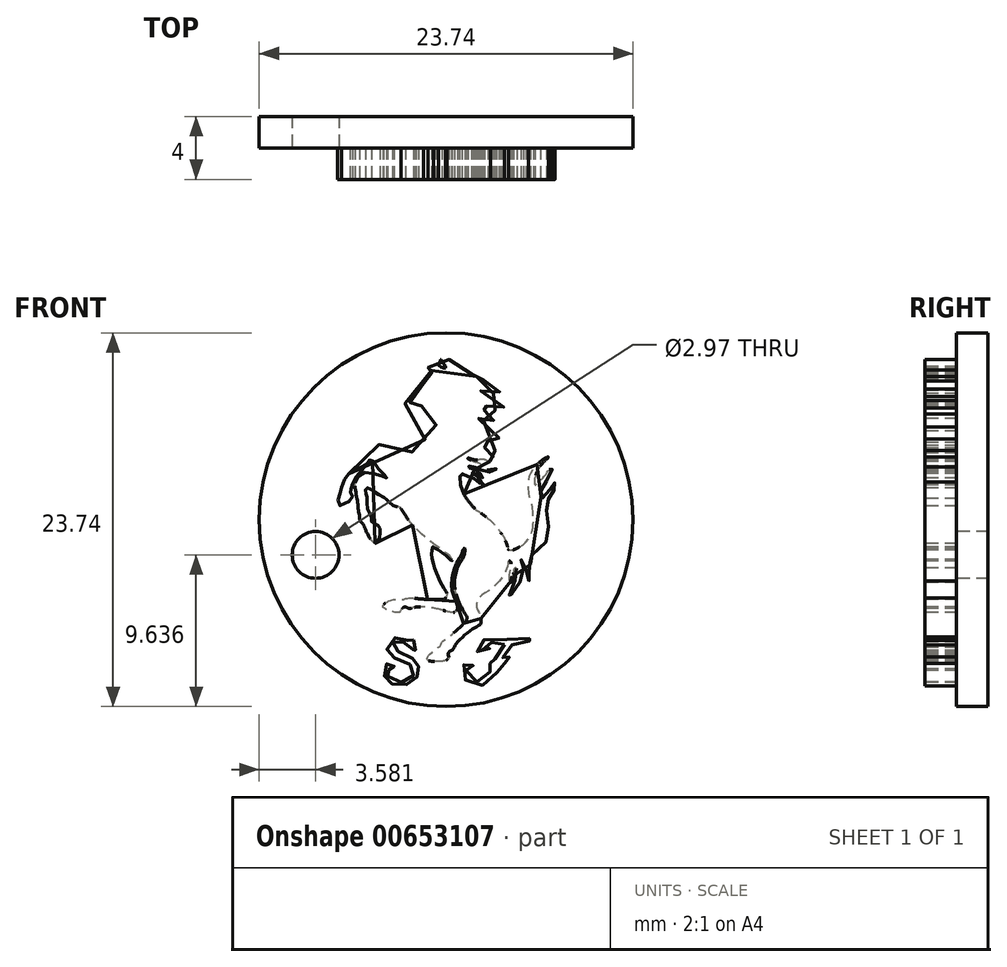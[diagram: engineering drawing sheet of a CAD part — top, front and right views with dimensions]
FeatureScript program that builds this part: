
annotation { "Feature Type Name" : "Feature", "Feature Type Description" : "" }
export const myFeature = defineFeature(function(context is Context, id is Id, definition is map)
    precondition{}
    {
        {
            var Q0;
            Q0=qCreatedBy(makeId("Front.planeOp"),FACE);
            var sketch = newSketch(context, id + "F0", { "sketchPlane" : qUnion([Q0])});
            skCircle(sketch, "E0", {"center": v(-6.3, 17.6) * mm, "radius": 11.87 * mm});
            skSolve(sketch);
        }
        {
            var Q0;
            Q0=qCreatedBy(makeId("Front.planeOp"),FACE);
            var sketch = newSketch(context, id + "F1", { "sketchPlane" : qUnion([Q0])});
            skFitSpline(sketch, "E1", {"points": [v(-12.5, 20.52) * mm, v(-12.32, 20.83) * mm, v(-12.29, 20.92) * mm, v(-11.96, 21.5) * mm, v(-11.74, 21.89) * mm, v(-11.58, 22.13) * mm, v(-11.5, 22.28) * mm, v(-11.38, 22.4) * mm, v(-11.23, 22.5) * mm, v(-11.09, 22.52) * mm, v(-11, 22.52) * mm, v(-10.9, 22.5) * mm, v(-10.7, 22.45) * mm, v(-10.6, 22.38) * mm, v(-10.51, 22.33) * mm, v(-10.41, 22.25) * mm, v(-10.33, 22.16) * mm, v(-10.27, 22.08) * mm, v(-10.24, 22.05) * mm, v(-10.22, 22.03) * mm, v(-10.1, 21.96) * mm, v(-9.68, 21.67) * mm, v(-9.47, 21.52) * mm, v(-9.3, 21.41) * mm, v(-9.27, 21.38) * mm, v(-9.25, 21.37) * mm, v(-9.24, 21.38) * mm, v(-9.06, 21.53) * mm, v(-8.92, 21.64) * mm, v(-8.83, 21.7) * mm, v(-8.55, 21.86) * mm, v(-8.37, 21.93) * mm, v(-8.25, 22) * mm, v(-8.17, 22.07) * mm, v(-8.05, 22.2) * mm, v(-7.95, 22.35) * mm, v(-7.9, 22.42) * mm, v(-7.84, 22.5) * mm, v(-7.77, 22.57) * mm, v(-7.75, 22.6) * mm, v(-7.62, 22.7) * mm, v(-7.51, 22.82) * mm, v(-7.47, 22.88) * mm, v(-7.3, 23.07) * mm, v(-7.18, 23.22) * mm, v(-7.1, 23.34) * mm, v(-7.01, 23.47) * mm, v(-6.9, 23.7) * mm, v(-6.8, 23.89) * mm, v(-6.65, 24.26) * mm, v(-6.6, 24.4) * mm, v(-6.57, 24.48) * mm, v(-6.57, 24.56) * mm, v(-6.59, 24.6) * mm, v(-6.63, 24.66) * mm, v(-6.67, 24.69) * mm, v(-6.75, 24.66) * mm, v(-6.88, 24.64) * mm, v(-6.89, 24.64) * mm, v(-7.03, 24.64) * mm, v(-7.24, 24.7) * mm, v(-7.32, 24.71) * mm, v(-7.62, 24.8) * mm, v(-7.8, 24.82) * mm, v(-7.81, 24.82) * mm, v(-7.9, 24.83) * mm, v(-8.1, 24.84) * mm, v(-8.32, 24.76) * mm, v(-8.43, 24.7) * mm, v(-8.54, 24.68) * mm, v(-8.67, 24.68) * mm, v(-8.76, 24.71) * mm, v(-8.85, 24.78) * mm, v(-8.87, 24.83) * mm, v(-8.83, 24.88) * mm, v(-8.76, 24.9) * mm, v(-8.7, 24.9) * mm, v(-8.57, 24.94) * mm, v(-8.45, 24.98) * mm, v(-8.38, 25.02) * mm, v(-8.36, 25.06) * mm, v(-8.37, 25.09) * mm, v(-8.4, 25.1) * mm, v(-8.45, 25.11) * mm, v(-8.5, 25.1) * mm, v(-8.63, 25.05) * mm, v(-8.92, 24.98) * mm, v(-9.08, 24.98) * mm, v(-9.1, 24.99) * mm, v(-9.14, 25.03) * mm, v(-9.16, 25.11) * mm, v(-9.17, 25.2) * mm, v(-9.18, 25.36) * mm, v(-9.12, 25.5) * mm, v(-8.97, 25.73) * mm, v(-8.88, 25.87) * mm, v(-8.68, 25.99) * mm, v(-8.43, 26.02) * mm, v(-8.22, 26.07) * mm, v(-7.93, 26.18) * mm, v(-7.63, 26.3) * mm, v(-7.48, 26.39) * mm, v(-7.25, 26.53) * mm, v(-7.08, 26.62) * mm, v(-6.95, 26.67) * mm, v(-6.86, 26.7) * mm, v(-6.82, 26.7) * mm, v(-6.8, 26.73) * mm, v(-6.8, 26.75) * mm, v(-6.81, 26.77) * mm, v(-6.84, 26.77) * mm, v(-6.93, 26.77) * mm, v(-6.98, 26.76) * mm, v(-7, 26.77) * mm, v(-7, 26.8) * mm, v(-6.98, 26.81) * mm, v(-6.95, 26.82) * mm, v(-6.91, 26.83) * mm, v(-6.9, 26.86) * mm, v(-6.9, 26.88) * mm, v(-6.91, 26.88) * mm, v(-6.95, 26.88) * mm, v(-7, 26.88) * mm, v(-7.05, 26.88) * mm, v(-7.1, 26.9) * mm, v(-7.24, 26.95) * mm, v(-7.36, 26.98) * mm, v(-7.43, 27) * mm, v(-7.5, 27) * mm, v(-7.67, 26.97) * mm, v(-7.7, 26.96) * mm, v(-7.73, 26.96) * mm, v(-7.74, 26.97) * mm, v(-7.75, 27) * mm, v(-7.75, 27.02) * mm, v(-7.7, 27.04) * mm, v(-7.63, 27.07) * mm, v(-7.54, 27.1) * mm, v(-7.34, 27.1) * mm, v(-7.28, 27.08) * mm, v(-7.2, 27.09) * mm, v(-7.16, 27.1) * mm, v(-7.12, 27.13) * mm, v(-7.12, 27.14) * mm, v(-7.12, 27.14) * mm, v(-7.14, 27.15) * mm, v(-7.17, 27.16) * mm, v(-7.24, 27.16) * mm, v(-7.28, 27.18) * mm, v(-7.42, 27.22) * mm, v(-7.44, 27.24) * mm, v(-7.44, 27.27) * mm, v(-7.42, 27.28) * mm, v(-7.38, 27.28) * mm, v(-7.32, 27.29) * mm, v(-7.27, 27.29) * mm, v(-7.2, 27.3) * mm, v(-7.1, 27.32) * mm, v(-6.98, 27.32) * mm, v(-6.87, 27.3) * mm, v(-6.77, 27.27) * mm, v(-6.66, 27.22) * mm, v(-6.48, 27.14) * mm, v(-6.34, 27.12) * mm, v(-6.25, 27.13) * mm, v(-6.18, 27.18) * mm, v(-6.16, 27.2) * mm, v(-6.17, 27.26) * mm, v(-6.23, 27.34) * mm, v(-6.23, 27.5) * mm, v(-6.19, 27.59) * mm, v(-6.12, 27.78) * mm, v(-6.12, 27.79) * mm, v(-6.1, 27.78) * mm, v(-6.07, 27.74) * mm, v(-5.99, 27.64) * mm, v(-5.88, 27.57) * mm, v(-5.8, 27.5) * mm, v(-5.77, 27.48) * mm, v(-5.68, 27.41) * mm, v(-5.59, 27.32) * mm, v(-5.52, 27.25) * mm, v(-5.47, 27.18) * mm, v(-5.45, 27.14) * mm, v(-5.44, 27.12) * mm, v(-5.42, 27.12) * mm, v(-5.28, 27.12) * mm, v(-5.27, 27.12) * mm, v(-5.11, 27.1) * mm, v(-5.1, 27.1) * mm, v(-5.04, 27.1) * mm, v(-5, 27.07) * mm, v(-4.9, 27.02) * mm, v(-4.8, 26.94) * mm, v(-4.79, 26.93) * mm, v(-4.71, 26.85) * mm, v(-4.62, 26.74) * mm, v(-4.57, 26.72) * mm, v(-4.5, 26.7) * mm, v(-4.37, 26.7) * mm, v(-4.12, 26.7) * mm, v(-3.95, 26.7) * mm, v(-3.8, 26.7) * mm, v(-3.7, 26.67) * mm, v(-3.64, 26.63) * mm, v(-3.53, 26.56) * mm, v(-3.5, 26.52) * mm, v(-3.5, 26.49) * mm, v(-3.5, 26.46) * mm, v(-3.52, 26.43) * mm, v(-3.57, 26.42) * mm, v(-3.64, 26.45) * mm, v(-3.7, 26.48) * mm, v(-3.73, 26.5) * mm, v(-3.77, 26.5) * mm, v(-3.83, 26.5) * mm, v(-3.87, 26.48) * mm, v(-3.94, 26.46) * mm, v(-4, 26.44) * mm, v(-4.26, 26.36) * mm, v(-4.3, 26.33) * mm, v(-4.32, 26.32) * mm, v(-4.32, 26.3) * mm, v(-4.3, 26.29) * mm, v(-4.28, 26.28) * mm, v(-4.2, 26.27) * mm, v(-4.2, 26.27) * mm, v(-4.13, 26.25) * mm, v(-4.02, 26.22) * mm, v(-3.87, 26.15) * mm, v(-3.76, 26.08) * mm, v(-3.65, 26) * mm, v(-3.54, 25.94) * mm, v(-3.5, 25.92) * mm, v(-3.42, 25.91) * mm, v(-3.3, 25.9) * mm, v(-3.14, 25.86) * mm, v(-3.03, 25.8) * mm, v(-2.92, 25.72) * mm, v(-2.86, 25.67) * mm, v(-2.86, 25.67) * mm, v(-2.79, 25.6) * mm, v(-2.78, 25.6) * mm, v(-2.72, 25.57) * mm, v(-2.66, 25.53) * mm, v(-2.62, 25.5) * mm, v(-2.6, 25.47) * mm, v(-2.6, 25.46) * mm, v(-2.62, 25.44) * mm, v(-2.65, 25.44) * mm, v(-2.72, 25.45) * mm, v(-2.82, 25.49) * mm, v(-2.9, 25.54) * mm, v(-2.99, 25.59) * mm, v(-3.02, 25.6) * mm, v(-3.07, 25.62) * mm, v(-3.16, 25.62) * mm, v(-3.16, 25.62) * mm, v(-3.25, 25.62) * mm, v(-3.39, 25.6) * mm, v(-3.63, 25.62) * mm, v(-3.98, 25.74) * mm, v(-4.19, 25.8) * mm, v(-4.3, 25.8) * mm, v(-4.3, 25.8) * mm, v(-4.31, 25.76) * mm, v(-4.28, 25.7) * mm, v(-4.16, 25.64) * mm, v(-4, 25.56) * mm, v(-3.93, 25.52) * mm, v(-3.81, 25.41) * mm, v(-3.75, 25.32) * mm, v(-3.67, 25.24) * mm, v(-3.51, 25.18) * mm, v(-3.32, 25.17) * mm, v(-3.07, 25.1) * mm, v(-2.85, 24.98) * mm, v(-2.78, 24.92) * mm, v(-2.68, 24.82) * mm, v(-2.64, 24.75) * mm, v(-2.65, 24.72) * mm, v(-2.67, 24.68) * mm, v(-2.7, 24.68) * mm, v(-2.72, 24.7) * mm, v(-2.77, 24.77) * mm, v(-2.83, 24.83) * mm, v(-2.92, 24.9) * mm, v(-3.02, 24.93) * mm, v(-3.12, 24.94) * mm, v(-3.23, 24.9) * mm, v(-3.45, 24.88) * mm, v(-3.57, 24.9) * mm, v(-3.75, 24.98) * mm, v(-3.88, 25.09) * mm, v(-3.9, 25.1) * mm, v(-3.94, 25.12) * mm, v(-3.95, 25.12) * mm, v(-3.96, 25.1) * mm, v(-3.96, 25.06) * mm, v(-3.9, 25) * mm, v(-3.76, 24.86) * mm, v(-3.76, 24.85) * mm, v(-3.65, 24.75) * mm, v(-3.57, 24.7) * mm, v(-3.51, 24.7) * mm, v(-3.41, 24.66) * mm, v(-3.27, 24.6) * mm, v(-3.15, 24.53) * mm, v(-3.1, 24.49) * mm, v(-3.07, 24.47) * mm, v(-3.02, 24.46) * mm, v(-2.97, 24.45) * mm, v(-2.89, 24.45) * mm, v(-2.88, 24.44) * mm, v(-2.87, 24.42) * mm, v(-2.88, 24.39) * mm, v(-2.9, 24.37) * mm, v(-2.97, 24.33) * mm, v(-3.13, 24.33) * mm, v(-3.26, 24.38) * mm, v(-3.5, 24.45) * mm, v(-3.7, 24.5) * mm, v(-3.93, 24.6) * mm, v(-4.07, 24.68) * mm, v(-4.13, 24.7) * mm, v(-4.25, 24.7) * mm, v(-4.3, 24.68) * mm, v(-4.3, 24.68) * mm, v(-4.32, 24.65) * mm, v(-4.32, 24.62) * mm, v(-4.28, 24.6) * mm, v(-4.22, 24.57) * mm, v(-4.12, 24.55) * mm, v(-4.05, 24.53) * mm, v(-3.97, 24.5) * mm, v(-3.87, 24.44) * mm, v(-3.73, 24.36) * mm, v(-3.65, 24.3) * mm, v(-3.59, 24.23) * mm, v(-3.55, 24.14) * mm, v(-3.5, 24.07) * mm, v(-3.46, 24.01) * mm, v(-3.4, 23.98) * mm, v(-3.32, 23.93) * mm, v(-3.26, 23.89) * mm, v(-3.22, 23.84) * mm, v(-3.18, 23.79) * mm, v(-3.15, 23.73) * mm, v(-3.1, 23.68) * mm, v(-2.98, 23.62) * mm, v(-2.9, 23.6) * mm, v(-2.86, 23.55) * mm, v(-2.84, 23.5) * mm, v(-2.84, 23.5) * mm, v(-3.08, 23.5) * mm, v(-3.3, 23.65) * mm, v(-3.36, 23.7) * mm, v(-3.61, 23.77) * mm, v(-3.72, 23.81) * mm, v(-3.86, 23.88) * mm, v(-3.99, 23.94) * mm, v(-4.15, 24) * mm, v(-4.19, 24.03) * mm, v(-4.25, 24.04) * mm, v(-4.28, 24.03) * mm, v(-4.28, 24) * mm, v(-4.25, 23.94) * mm, v(-4.15, 23.82) * mm, v(-4.05, 23.74) * mm, v(-3.91, 23.65) * mm, v(-3.8, 23.58) * mm, v(-3.74, 23.54) * mm, v(-3.62, 23.43) * mm, v(-3.54, 23.32) * mm, v(-3.5, 23.25) * mm, v(-3.5, 23.18) * mm, v(-3.48, 23.13) * mm, v(-3.42, 23.05) * mm, v(-3.33, 23) * mm, v(-3.23, 22.95) * mm, v(-3.1, 22.92) * mm, v(-3, 22.88) * mm, v(-2.95, 22.8) * mm, v(-2.95, 22.78) * mm, v(-2.98, 22.76) * mm, v(-3.29, 22.74) * mm, v(-3.6, 22.9) * mm, v(-3.75, 23.06) * mm, v(-3.87, 23.12) * mm, v(-4.06, 23.15) * mm, v(-4.25, 23.23) * mm, v(-4.4, 23.23) * mm, v(-4.43, 23.2) * mm, v(-4.44, 23.16) * mm, v(-4.32, 23.1) * mm, v(-4.17, 23.03) * mm, v(-4, 22.82) * mm, v(-3.84, 22.7) * mm, v(-3.66, 22.61) * mm, v(-3.53, 22.5) * mm, v(-3.41, 22.33) * mm, v(-3.33, 22.22) * mm, v(-3.33, 22.19) * mm, v(-3.24, 22.09) * mm, v(-3.2, 22.05) * mm, v(-3.18, 22.02) * mm, v(-3.23, 22) * mm, v(-3.31, 22) * mm, v(-3.46, 22.15) * mm, v(-3.52, 22.2) * mm, v(-3.7, 22.27) * mm, v(-4.11, 22.48) * mm, v(-4.17, 22.5) * mm, v(-4.17, 22.47) * mm, v(-4.1, 22.37) * mm, v(-3.96, 22.27) * mm, v(-3.87, 22.2) * mm, v(-3.85, 22.17) * mm, v(-3.87, 22.15) * mm, v(-3.92, 22.14) * mm, v(-4, 22.15) * mm, v(-4.07, 22.19) * mm, v(-4.13, 22.23) * mm, v(-4.3, 22.3) * mm, v(-4.36, 22.3) * mm, v(-4.38, 22.3) * mm, v(-4.38, 22.28) * mm, v(-4.33, 22.2) * mm, v(-4.15, 22.1) * mm, v(-3.94, 22.06) * mm, v(-3.83, 22.01) * mm, v(-3.72, 21.93) * mm, v(-3.55, 21.8) * mm, v(-3.4, 21.74) * mm, v(-3.3, 21.72) * mm, v(-3.28, 21.69) * mm, v(-3.28, 21.62) * mm, v(-3.37, 21.6) * mm, v(-3.58, 21.62) * mm, v(-3.8, 21.67) * mm, v(-3.95, 21.77) * mm, v(-4.12, 21.83) * mm, v(-4.28, 21.83) * mm, v(-4.4, 21.8) * mm, v(-4.4, 21.77) * mm, v(-4.36, 21.75) * mm, v(-4.19, 21.74) * mm, v(-4.04, 21.7) * mm, v(-3.94, 21.67) * mm, v(-3.83, 21.6) * mm, v(-3.7, 21.47) * mm, v(-3.54, 21.35) * mm, v(-3.52, 21.32) * mm, v(-3.54, 21.3) * mm, v(-3.57, 21.28) * mm, v(-3.67, 21.32) * mm, v(-3.82, 21.4) * mm, v(-4.01, 21.43) * mm, v(-4.2, 21.4) * mm, v(-4.49, 21.4) * mm, v(-4.78, 21.48) * mm, v(-4.88, 21.52) * mm, v(-4.91, 21.52) * mm, v(-4.92, 21.5) * mm, v(-4.92, 21.47) * mm, v(-4.9, 21.45) * mm, v(-4.79, 21.4) * mm, v(-4.64, 21.34) * mm, v(-4.47, 21.27) * mm, v(-4.24, 21.2) * mm, v(-4.03, 21.06) * mm, v(-3.93, 20.95) * mm, v(-3.8, 20.82) * mm, v(-3.65, 20.75) * mm, v(-3.43, 20.76) * mm, v(-3.28, 20.8) * mm, v(-3.16, 20.88) * mm, v(-3.12, 20.9) * mm, v(-3.1, 20.89) * mm, v(-3.1, 20.87) * mm, v(-3.12, 20.81) * mm, v(-3.31, 20.68) * mm, v(-3.57, 20.63) * mm, v(-3.88, 20.67) * mm, v(-4.13, 20.79) * mm, v(-4.3, 20.86) * mm, v(-4.33, 20.86) * mm, v(-4.43, 20.9) * mm, v(-4.65, 20.94) * mm, v(-4.77, 20.97) * mm, v(-4.87, 21) * mm, v(-4.93, 21.01) * mm, v(-4.95, 21.01) * mm, v(-4.94, 20.98) * mm, v(-4.8, 20.9) * mm, v(-4.78, 20.9) * mm, v(-4.67, 20.86) * mm, v(-4.55, 20.82) * mm, v(-4.37, 20.72) * mm, v(-4.25, 20.63) * mm, v(-4.16, 20.54) * mm, v(-4, 20.4) * mm, v(-3.97, 20.36) * mm, v(-3.98, 20.27) * mm, v(-4, 20.26) * mm, v(-4.06, 20.29) * mm, v(-4.2, 20.4) * mm, v(-4.33, 20.5) * mm, v(-4.48, 20.55) * mm, v(-4.58, 20.57) * mm, v(-4.65, 20.58) * mm, v(-4.67, 20.58) * mm, v(-4.69, 20.56) * mm, v(-4.7, 20.54) * mm, v(-4.65, 20.51) * mm, v(-4.58, 20.5) * mm, v(-4.5, 20.47) * mm, v(-4.4, 20.4) * mm, v(-4.3, 20.3) * mm, v(-4.23, 20.22) * mm, v(-4.2, 20.16) * mm, v(-4.17, 20.1) * mm, v(-4.1, 20.02) * mm, v(-4.02, 19.95) * mm, v(-3.97, 19.94) * mm, v(-3.95, 19.92) * mm, v(-3.95, 19.9) * mm, v(-3.96, 19.87) * mm, v(-4, 19.85) * mm, v(-4.05, 19.86) * mm, v(-4.11, 19.9) * mm, v(-4.23, 19.98) * mm, v(-4.4, 20.12) * mm, v(-4.53, 20.21) * mm, v(-4.7, 20.3) * mm, v(-4.82, 20.34) * mm, v(-4.94, 20.34) * mm, v(-5.08, 20.38) * mm, v(-5.23, 20.5) * mm, v(-5.3, 20.53) * mm, v(-5.36, 20.55) * mm, v(-5.39, 20.51) * mm, v(-5.42, 20.37) * mm, v(-5.44, 20.11) * mm, v(-5.4, 19.82) * mm, v(-5.24, 19.38) * mm, v(-5.06, 19.02) * mm, v(-4.38, 18.2) * mm, v(-4.3, 18.16) * mm, v(-3.6, 17.64) * mm, v(-3.3, 17.37) * mm, v(-2.72, 16.62) * mm, v(-2.47, 16.11) * mm, v(-2.36, 15.7) * mm, v(-2.35, 15.68) * mm, v(-2.12, 15.67) * mm, v(-1.6, 15.9) * mm, v(-1.29, 16.11) * mm, v(-0.96, 16.53) * mm, v(-0.81, 16.98) * mm, v(-0.78, 17.26) * mm, v(-0.76, 17.62) * mm, v(-0.8, 18.22) * mm, v(-0.89, 18.71) * mm, v(-0.98, 18.97) * mm, v(-1.08, 19.51) * mm, v(-1.06, 20.03) * mm, v(-0.98, 20.43) * mm, v(-0.81, 20.74) * mm, v(-0.51, 21.12) * mm, v(-0.25, 21.33) * mm, v(-0.1, 21.45) * mm, v(0.1, 21.58) * mm, v(0.14, 21.6) * mm, v(0.17, 21.59) * mm, v(0.18, 21.57) * mm, v(0.19, 21.55) * mm, v(0.16, 21.52) * mm, v(0.03, 21.4) * mm, v(-0.15, 21.22) * mm, v(-0.31, 21) * mm, v(-0.41, 20.86) * mm, v(-0.52, 20.66) * mm, v(-0.65, 20.33) * mm, v(-0.68, 20.2) * mm, v(-0.67, 19.85) * mm, v(-0.67, 19.82) * mm, v(-0.66, 19.81) * mm, v(-0.63, 19.81) * mm, v(-0.6, 19.84) * mm, v(-0.34, 20.07) * mm, v(-0.1, 20.3) * mm, v(0.05, 20.5) * mm, v(0.14, 20.64) * mm, v(0.3, 20.9) * mm, v(0.35, 20.95) * mm, v(0.37, 20.96) * mm, v(0.4, 20.95) * mm, v(0.41, 20.94) * mm, v(0.42, 20.9) * mm, v(0.43, 20.87) * mm, v(0.43, 20.82) * mm, v(0.42, 20.73) * mm, v(0.37, 20.55) * mm, v(0.28, 20.38) * mm, v(0.02, 20) * mm, v(-0.09, 19.86) * mm, v(-0.17, 19.73) * mm, v(-0.24, 19.57) * mm, v(-0.29, 19.4) * mm, v(-0.3, 19.32) * mm, v(-0.3, 19.2) * mm, v(-0.28, 19.07) * mm, v(-0.24, 19) * mm, v(-0.21, 18.96) * mm, v(-0.14, 18.96) * mm, v(-0.01, 19.08) * mm, v(0.22, 19.4) * mm, v(0.33, 19.56) * mm, v(0.4, 19.72) * mm, v(0.5, 19.95) * mm, v(0.53, 20) * mm, v(0.54, 20) * mm, v(0.58, 19.96) * mm, v(0.6, 19.9) * mm, v(0.6, 19.9) * mm, v(0.61, 19.82) * mm, v(0.61, 19.74) * mm, v(0.6, 19.67) * mm, v(0.58, 19.56) * mm, v(0.5, 19.4) * mm, v(0.37, 19.2) * mm, v(0.27, 19.07) * mm, v(0.2, 18.94) * mm, v(0.19, 18.92) * mm, v(0.15, 18.81) * mm, v(0.14, 18.8) * mm, v(0.13, 18.7) * mm, v(0.09, 18.38) * mm, v(0.1, 17.93) * mm, v(0.18, 17.51) * mm, v(0.21, 17.21) * mm, v(0.19, 16.83) * mm, v(0.15, 16.5) * mm, v(0, 16.12) * mm, v(-0.32, 15.69) * mm, v(-0.83, 15.37) * mm, v(-1.1, 15.27) * mm, v(-1.1, 15.26) * mm, v(-1.1, 15.24) * mm, v(-1.07, 15.18) * mm, v(-1, 15) * mm, v(-0.95, 14.7) * mm, v(-0.96, 14.56) * mm, v(-0.98, 14.43) * mm, v(-1.04, 14.34) * mm, v(-1.05, 14.21) * mm, v(-1.04, 14.04) * mm, v(-1, 13.94) * mm, v(-1, 13.73) * mm, v(-1, 13.72) * mm, v(-1.01, 13.71) * mm, v(-1.04, 13.74) * mm, v(-1.13, 13.88) * mm, v(-1.2, 14.08) * mm, v(-1.24, 14.4) * mm, v(-1.24, 14.6) * mm, v(-1.35, 14.9) * mm, v(-1.49, 15.07) * mm, v(-1.52, 15.08) * mm, v(-1.54, 15.07) * mm, v(-1.55, 15.03) * mm, v(-1.54, 14.97) * mm, v(-1.46, 14.85) * mm, v(-1.4, 14.73) * mm, v(-1.39, 14.53) * mm, v(-1.4, 14.29) * mm, v(-1.45, 14) * mm, v(-1.63, 13.58) * mm, v(-1.88, 13.26) * mm, v(-2.02, 13.08) * mm, v(-2.13, 12.89) * mm, v(-2.15, 12.75) * mm, v(-2.14, 12.64) * mm, v(-2.14, 12.63) * mm, v(-2.16, 12.63) * mm, v(-2.2, 12.69) * mm, v(-2.28, 12.8) * mm, v(-2.3, 13) * mm, v(-2.09, 13.43) * mm, v(-1.91, 13.78) * mm, v(-1.82, 14.02) * mm, v(-1.81, 14.26) * mm, v(-1.84, 14.47) * mm, v(-1.86, 14.53) * mm, v(-1.9, 14.53) * mm, v(-1.94, 14.51) * mm, v(-1.99, 14.46) * mm, v(-2.01, 14.4) * mm, v(-2.03, 14.3) * mm, v(-2.03, 14.2) * mm, v(-2.1, 14.02) * mm, v(-2.15, 13.9) * mm, v(-2.17, 13.74) * mm, v(-2.19, 13.64) * mm, v(-2.2, 13.6) * mm, v(-2.21, 13.6) * mm, v(-2.24, 13.67) * mm, v(-2.28, 13.88) * mm, v(-2.27, 14.12) * mm, v(-2.2, 14.41) * mm, v(-2.17, 14.63) * mm, v(-2.17, 14.77) * mm, v(-2.2, 14.91) * mm, v(-2.24, 14.96) * mm, v(-2.28, 14.99) * mm, v(-2.36, 14.97) * mm, v(-2.37, 14.9) * mm, v(-2.4, 14.7) * mm, v(-2.47, 14.44) * mm, v(-2.6, 14.15) * mm, v(-2.9, 13.72) * mm, v(-3.24, 13.4) * mm, v(-3.67, 13.05) * mm, v(-4.08, 12.78) * mm, v(-4.33, 12.44) * mm, v(-4.37, 12.03) * mm, v(-4.23, 11.71) * mm, v(-4.11, 11.5) * mm, v(-4.09, 11.38) * mm, v(-4.1, 11.03) * mm, v(-4.16, 10.92) * mm, v(-4.33, 10.83) * mm, v(-4.53, 10.72) * mm, v(-4.7, 10.6) * mm, v(-5.03, 10.35) * mm, v(-5.32, 10.08) * mm, v(-5.56, 9.83) * mm, v(-5.73, 9.63) * mm, v(-5.76, 9.52) * mm, v(-5.79, 9.47) * mm, v(-5.88, 9.34) * mm, v(-6, 9.27) * mm, v(-6.07, 9.24) * mm, v(-6.14, 9.18) * mm, v(-6.18, 9.09) * mm, v(-6.16, 8.99) * mm, v(-6.13, 8.9) * mm, v(-6.12, 8.85) * mm, v(-6.15, 8.78) * mm, v(-6.34, 8.66) * mm, v(-6.75, 8.58) * mm, v(-7.18, 8.6) * mm, v(-7.5, 8.69) * mm, v(-7.4, 8.98) * mm, v(-6.93, 9.39) * mm, v(-6.74, 9.52) * mm, v(-6.65, 9.63) * mm, v(-6.58, 9.8) * mm, v(-6.34, 10.01) * mm, v(-5.82, 10.4) * mm, v(-5.4, 10.8) * mm, v(-5.08, 11.11) * mm, v(-5, 11.23) * mm, v(-4.99, 11.27) * mm, v(-4.97, 11.32) * mm, v(-4.98, 11.43) * mm, v(-5, 11.45) * mm, v(-5.19, 11.77) * mm, v(-5.23, 11.84) * mm, v(-5.42, 12.22) * mm, v(-5.46, 12.32) * mm, v(-5.65, 12.84) * mm, v(-5.74, 13.27) * mm, v(-5.77, 13.55) * mm, v(-5.7, 14.12) * mm, v(-5.57, 14.6) * mm, v(-5.47, 14.77) * mm, v(-5.3, 15.04) * mm, v(-5.14, 15.41) * mm, v(-5.1, 15.59) * mm, v(-5.11, 15.73) * mm, v(-5.13, 15.79) * mm, v(-5.16, 15.8) * mm, v(-5.2, 15.77) * mm, v(-5.24, 15.6) * mm, v(-5.31, 15.39) * mm, v(-5.54, 15) * mm, v(-5.73, 14.64) * mm, v(-5.86, 14.25) * mm, v(-5.93, 13.93) * mm, v(-5.94, 13.38) * mm, v(-5.88, 12.95) * mm, v(-5.68, 12.43) * mm, v(-5.6, 12.2) * mm, v(-5.57, 12.1) * mm, v(-5.59, 11.93) * mm, v(-5.64, 11.85) * mm, v(-5.66, 11.79) * mm, v(-5.75, 11.72) * mm, v(-6.08, 11.73) * mm, v(-6.36, 11.8) * mm, v(-6.93, 11.95) * mm, v(-7.7, 12.06) * mm, v(-8.27, 12.04) * mm, v(-8.5, 11.98) * mm, v(-8.62, 11.97) * mm, v(-8.76, 12) * mm, v(-8.86, 12.05) * mm, v(-8.94, 12.05) * mm, v(-9, 12.04) * mm, v(-9.08, 11.96) * mm, v(-9.22, 11.76) * mm, v(-9.27, 11.71) * mm, v(-9.57, 11.73) * mm, v(-10.11, 11.92) * mm, v(-10.32, 12.1) * mm, v(-10.17, 12.3) * mm, v(-9.6, 12.52) * mm, v(-9.06, 12.54) * mm, v(-8.86, 12.59) * mm, v(-8.55, 12.63) * mm, v(-8.27, 12.61) * mm, v(-7.99, 12.57) * mm, v(-7.73, 12.55) * mm, v(-6.62, 12.53) * mm, v(-6.44, 12.55) * mm, v(-6.32, 12.65) * mm, v(-6.23, 12.82) * mm, v(-6.26, 12.97) * mm, v(-6.5, 13.33) * mm, v(-6.74, 13.8) * mm, v(-6.8, 13.93) * mm, v(-7.06, 14.6) * mm, v(-7.17, 15.04) * mm, v(-7.22, 15.37) * mm, v(-7.17, 15.87) * mm, v(-7.16, 15.88) * mm, v(-7.14, 15.88) * mm, v(-7.06, 15.83) * mm, v(-6.76, 15.65) * mm, v(-6.43, 15.4) * mm, v(-6.1, 15.12) * mm, v(-5.99, 15.01) * mm, v(-5.92, 15) * mm, v(-5.93, 15.09) * mm, v(-5.97, 15.16) * mm, v(-6.08, 15.3) * mm, v(-6.22, 15.43) * mm, v(-6.43, 15.57) * mm, v(-6.66, 15.74) * mm, v(-7.02, 16) * mm, v(-7.67, 16.53) * mm, v(-8.16, 16.97) * mm, v(-8.67, 17.54) * mm, v(-9.22, 18.36) * mm, v(-9.28, 18.4) * mm, v(-9.48, 18.44) * mm, v(-9.7, 18.53) * mm, v(-9.94, 18.73) * mm, v(-10, 18.83) * mm, v(-10.12, 18.92) * mm, v(-10.18, 18.96) * mm, v(-10.42, 19.11) * mm, v(-10.9, 19.4) * mm, v(-11.04, 19.5) * mm, v(-11.15, 19.58) * mm, v(-11.24, 19.62) * mm, v(-11.34, 19.61) * mm, v(-11.41, 19.54) * mm, v(-11.43, 19.46) * mm, v(-11.38, 19.23) * mm, v(-11.35, 19.12) * mm, v(-11.33, 18.95) * mm, v(-11.3, 18.44) * mm, v(-11.26, 18.2) * mm, v(-11.16, 18) * mm, v(-11.05, 17.78) * mm, v(-11.04, 17.53) * mm, v(-11, 17.42) * mm, v(-10.77, 17.31) * mm, v(-10.65, 17.26) * mm, v(-10.56, 17.18) * mm, v(-10.5, 17.02) * mm, v(-10.49, 16.82) * mm, v(-10.51, 16.52) * mm, v(-10.62, 16.23) * mm, v(-10.75, 16.12) * mm, v(-10.82, 16.1) * mm, v(-10.94, 16.19) * mm, v(-11.2, 16.54) * mm, v(-11.45, 17.04) * mm, v(-11.52, 17.23) * mm, v(-11.63, 17.38) * mm, v(-11.76, 17.55) * mm, v(-11.8, 17.8) * mm, v(-11.79, 17.85) * mm, v(-11.84, 18.01) * mm, v(-11.9, 18.54) * mm, v(-11.93, 18.74) * mm, v(-12.06, 19.54) * mm, v(-12.08, 19.99) * mm, v(-12.03, 20.12) * mm, v(-11.9, 20.33) * mm, v(-11.7, 20.5) * mm, v(-11.55, 20.6) * mm, v(-11.3, 20.6) * mm, v(-11.03, 20.55) * mm, v(-10.78, 20.5) * mm, v(-10.4, 20.39) * mm, v(-10.27, 20.34) * mm, v(-10.17, 20.29) * mm, v(-10.1, 20.26) * mm, v(-10.07, 20.25) * mm, v(-10.04, 20.25) * mm, v(-10.03, 20.27) * mm, v(-10.04, 20.31) * mm, v(-10.16, 20.41) * mm, v(-10.4, 20.62) * mm, v(-10.6, 20.82) * mm, v(-10.74, 21.01) * mm, v(-10.92, 21.28) * mm, v(-11, 21.37) * mm, v(-11.05, 21.38) * mm, v(-11.13, 21.38) * mm, v(-11.15, 21.38) * mm, v(-11.2, 21.39) * mm, v(-11.23, 21.36) * mm, v(-11.3, 21.25) * mm, v(-11.41, 21.05) * mm, v(-11.42, 21.04) * mm, v(-11.58, 20.84) * mm, v(-11.69, 20.7) * mm, v(-11.89, 20.49) * mm, v(-12.12, 20.18) * mm, v(-12.2, 20) * mm, v(-12.24, 19.84) * mm, v(-12.26, 19.72) * mm, v(-12.28, 19.65) * mm, v(-12.32, 19.58) * mm, v(-12.37, 19.5) * mm, v(-12.4, 19.45) * mm, v(-12.4, 19.41) * mm, v(-12.39, 19.35) * mm, v(-12.34, 19.27) * mm, v(-12.29, 19.18) * mm, v(-12.27, 19.14) * mm, v(-12.26, 19.1) * mm, v(-12.27, 19.01) * mm, v(-12.32, 18.93) * mm, v(-12.45, 18.8) * mm, v(-12.59, 18.7) * mm, v(-13, 18.5) * mm, v(-13.14, 18.5) * mm, v(-13.18, 18.55) * mm, v(-13.17, 18.91) * mm, v(-13.14, 19.02) * mm, v(-13.1, 19.2) * mm, v(-12.96, 19.45) * mm, v(-12.95, 19.5) * mm, v(-12.94, 19.62) * mm, v(-12.94, 19.74) * mm, v(-12.78, 20.1) * mm, v(-12.7, 20.19) * mm, v(-12.56, 20.42) * mm, v(-12.5, 20.52) * mm]});
            skFitSpline(sketch, "E2", {"points": [v(-6.41, 27.44) * mm, v(-6.36, 27.37) * mm, v(-6.35, 27.33) * mm, v(-6.34, 27.25) * mm, v(-6.35, 27.22) * mm, v(-6.41, 27.22) * mm, v(-6.54, 27.27) * mm, v(-6.73, 27.37) * mm, v(-6.77, 27.43) * mm, v(-6.76, 27.5) * mm, v(-6.71, 27.55) * mm, v(-6.68, 27.63) * mm, v(-6.66, 27.76) * mm, v(-6.65, 27.78) * mm, v(-6.54, 27.62) * mm, v(-6.41, 27.44) * mm]});
            skSolve(sketch);
        }
        {
            var Q0;
            Q0=makeQuery(id+"F1.imprint","IMPRINT",FACE,{"disambiguationData":[TD([[makeQuery(id+"F1.imprint","IMPRINT",EDGE,{"derivedFrom":sQuery(id+"F1.wireOp",EDGE,"E1")}),-1.0]])]});
            var Q1;
            Q1=makeQuery(id+"F1.imprint","IMPRINT",FACE,{"disambiguationData":[TD([[makeQuery(id+"F1.imprint","IMPRINT",EDGE,{"derivedFrom":sQuery(id+"F1.wireOp",EDGE,"ca44a590-de28-4ea7-9587-4d233c09eb77")}),1.0]])]});
            var Q2;
            Q2=makeQuery(id+"F1.imprint","IMPRINT",FACE,{"disambiguationData":[TD([[makeQuery(id+"F1.imprint","IMPRINT",EDGE,{"derivedFrom":sQuery(id+"F1.wireOp",EDGE,"E2")}),-1.0]])]});
            extrude(context, id + "F2", {"entities" : qUnion([Q0, Q1, Q2]), "depth" : 4 * mm, "offsetDistance" : 25 * mm});
        }
        {
            var Q0;
            Q0=qCreatedBy(makeId("Front.planeOp"),FACE);
            var sketch = newSketch(context, id + "F3", { "sketchPlane" : qUnion([Q0])});
            skFitSpline(sketch, "E3", {"points": [v(-8.39, 9.98) * mm, v(-8.38, 9.87) * mm, v(-8.35, 9.67) * mm, v(-8.3, 9.45) * mm, v(-8.21, 9.2) * mm, v(-8.21, 9.2) * mm, v(-8.22, 9.2) * mm, v(-8.23, 9.2) * mm, v(-8.27, 9.18) * mm, v(-8.27, 9.18) * mm, v(-8.28, 9.19) * mm, v(-8.3, 9.25) * mm, v(-8.4, 9.37) * mm, v(-8.56, 9.55) * mm, v(-8.8, 9.74) * mm, v(-9.04, 9.84) * mm, v(-9.2, 9.9) * mm, v(-9.49, 9.9) * mm, v(-9.63, 9.82) * mm, v(-9.7, 9.7) * mm, v(-9.7, 9.55) * mm, v(-9.54, 9.35) * mm, v(-9.2, 9.16) * mm, v(-8.73, 8.96) * mm, v(-8.38, 8.76) * mm, v(-8.24, 8.64) * mm, v(-8.14, 8.49) * mm, v(-8.08, 8.34) * mm, v(-8.06, 8.11) * mm, v(-8.06, 7.91) * mm, v(-8.12, 7.69) * mm, v(-8.24, 7.49) * mm, v(-8.49, 7.26) * mm, v(-8.77, 7.14) * mm, v(-9.13, 7.06) * mm, v(-9.53, 7.1) * mm, v(-9.9, 7.26) * mm, v(-10.04, 7.38) * mm, v(-10.14, 7.52) * mm, v(-10.25, 7.75) * mm, v(-10.28, 8.07) * mm, v(-10.16, 8.36) * mm, v(-9.98, 8.5) * mm, v(-9.78, 8.52) * mm, v(-9.67, 8.45) * mm, v(-9.61, 8.32) * mm, v(-9.62, 8.21) * mm, v(-9.66, 8.12) * mm, v(-9.75, 8.05) * mm, v(-9.88, 8.03) * mm, v(-9.97, 8.05) * mm, v(-10, 8.08) * mm, v(-10, 8.08) * mm, v(-10.02, 8.06) * mm, v(-10.05, 8.02) * mm, v(-10.06, 7.8) * mm, v(-9.89, 7.52) * mm, v(-9.6, 7.33) * mm, v(-9, 7.27) * mm, v(-8.61, 7.43) * mm, v(-8.42, 7.62) * mm, v(-8.35, 7.88) * mm, v(-8.36, 8.09) * mm, v(-8.54, 8.35) * mm, v(-9, 8.54) * mm, v(-9.5, 8.78) * mm, v(-9.78, 8.94) * mm, v(-9.96, 9.14) * mm, v(-10.04, 9.27) * mm, v(-10.07, 9.63) * mm, v(-9.85, 9.98) * mm, v(-9.34, 10.12) * mm, v(-8.92, 10) * mm, v(-8.78, 9.93) * mm, v(-8.65, 9.92) * mm, v(-8.55, 9.95) * mm, v(-8.49, 10.01) * mm, v(-8.43, 10.04) * mm, v(-8.4, 10.02) * mm, v(-8.39, 9.98) * mm]});
            skFitSpline(sketch, "E4", {"points": [v(-2.6, 9.66) * mm, v(-2.86, 9.38) * mm, v(-3.08, 9) * mm, v(-3.19, 8.76) * mm, v(-3.2, 8.75) * mm, v(-3.4, 8.7) * mm, v(-3.64, 8.46) * mm, v(-3.65, 8.46) * mm, v(-3.6, 8.4) * mm, v(-3.6, 8.4) * mm, v(-3.53, 8.45) * mm, v(-3.47, 8.49) * mm, v(-3.32, 8.5) * mm, v(-3.3, 8.5) * mm, v(-3.28, 8.48) * mm, v(-3.35, 8.3) * mm, v(-3.59, 7.83) * mm, v(-3.91, 7.49) * mm, v(-4.01, 7.4) * mm, v(-4.24, 7.31) * mm, v(-4.5, 7.3) * mm, v(-4.83, 7.45) * mm, v(-5.06, 7.8) * mm, v(-5.01, 8.13) * mm, v(-5, 8.13) * mm, v(-4.91, 8.07) * mm, v(-4.74, 8.07) * mm, v(-4.6, 8.21) * mm, v(-4.58, 8.36) * mm, v(-4.65, 8.48) * mm, v(-4.8, 8.56) * mm, v(-4.94, 8.55) * mm, v(-5.11, 8.46) * mm, v(-5.22, 8.3) * mm, v(-5.28, 8.02) * mm, v(-5.25, 7.7) * mm, v(-5.07, 7.4) * mm, v(-4.77, 7.15) * mm, v(-4.46, 7.06) * mm, v(-4, 7.08) * mm, v(-3.62, 7.27) * mm, v(-3.28, 7.6) * mm, v(-3.03, 7.96) * mm, v(-2.89, 8.27) * mm, v(-2.82, 8.5) * mm, v(-2.8, 8.5) * mm, v(-2.65, 8.48) * mm, v(-2.53, 8.5) * mm, v(-2.36, 8.6) * mm, v(-2.22, 8.78) * mm, v(-2.19, 8.82) * mm, v(-2.19, 8.83) * mm, v(-2.24, 8.85) * mm, v(-2.28, 8.87) * mm, v(-2.3, 8.84) * mm, v(-2.35, 8.8) * mm, v(-2.43, 8.76) * mm, v(-2.52, 8.74) * mm, v(-2.65, 8.74) * mm, v(-2.71, 8.75) * mm, v(-2.62, 9.01) * mm, v(-2.5, 9.28) * mm, v(-2.26, 9.65) * mm, v(-2.24, 9.66) * mm, v(-1.9, 9.66) * mm, v(-1.74, 9.69) * mm, v(-1.35, 9.78) * mm, v(-0.89, 9.95) * mm, v(-0.65, 10.06) * mm, v(-0.65, 10.07) * mm, v(-0.67, 10.13) * mm, v(-0.68, 10.14) * mm, v(-0.68, 10.14) * mm, v(-0.92, 10.07) * mm, v(-1.46, 9.97) * mm, v(-2.07, 9.93) * mm, v(-2.62, 10.01) * mm, v(-3.23, 10.1) * mm, v(-3.87, 9.98) * mm, v(-4.25, 9.72) * mm, v(-4.36, 9.52) * mm, v(-4.35, 9.36) * mm, v(-4.32, 9.23) * mm, v(-4.18, 9.1) * mm, v(-3.88, 9.07) * mm, v(-3.6, 9.25) * mm, v(-3.52, 9.45) * mm, v(-3.52, 9.46) * mm, v(-3.55, 9.47) * mm, v(-3.58, 9.47) * mm, v(-3.58, 9.46) * mm, v(-3.65, 9.38) * mm, v(-3.8, 9.32) * mm, v(-3.96, 9.32) * mm, v(-4.06, 9.42) * mm, v(-4.04, 9.6) * mm, v(-3.76, 9.8) * mm, v(-3.37, 9.8) * mm, v(-2.94, 9.71) * mm, v(-2.67, 9.68) * mm, v(-2.65, 9.67) * mm, v(-2.62, 9.67) * mm, v(-2.6, 9.67) * mm, v(-2.6, 9.67) * mm, v(-2.6, 9.67) * mm, v(-2.6, 9.66) * mm]});
            skSolve(sketch);
        }
        {
            var Q0;
            Q0=makeQuery(id+"F3.imprint","IMPRINT",FACE,{"disambiguationData":[TD([[makeQuery(id+"F3.imprint","IMPRINT",EDGE,{"derivedFrom":sQuery(id+"F3.wireOp",EDGE,"E3")}),-1.0]])]});
            var Q1;
            Q1=makeQuery(id+"F3.imprint","IMPRINT",FACE,{"disambiguationData":[TD([[makeQuery(id+"F3.imprint","IMPRINT",EDGE,{"derivedFrom":sQuery(id+"F3.wireOp",EDGE,"E4")}),1.0]])]});
            extrude(context, id + "F4", {"entities" : qUnion([Q0, Q1]), "operationType" : NewBodyOperationType.ADD, "depth" : 4 * mm, "offsetDistance" : 25 * mm});
        }
        {
            var Q0;
            Q0 = qSketchRegion(id + "F0", true);
            extrude(context, id + "F5", {"entities" : qUnion([Q0]), "operationType" : NewBodyOperationType.ADD, "depth" : 2 * mm, "offsetDistance" : 25 * mm});
        }
        {
            var Q0;
            Q0=makeQuery(id+"F5.opExtrude","CAP_FACE",FACE,{"disambiguationData":[OSD([sQuery(id+"F0.wireOp",EDGE,"E0")])],"isStart":false});
            var sketch = newSketch(context, id + "F6", { "sketchPlane" : qUnion([Q0])});
            skCircle(sketch, "E5", {"center": v(-14.59, 15.37) * mm, "radius": 1.49 * mm});
            skSolve(sketch);
        }
        {
            var Q0;
            Q0=makeQuery(id+"F6.imprint","IMPRINT",FACE,{"disambiguationData":[TD([[makeQuery(id+"F6.imprint","IMPRINT",EDGE,{"derivedFrom":sQuery(id+"F6.wireOp",EDGE,"E5")}),1.0]])]});
            extrude(context, id + "F7", {"entities" : qUnion([Q0]), "operationType" : NewBodyOperationType.REMOVE, "oppositeDirection" : true, "depth" : 25 * mm, "offsetDistance" : 25 * mm});
        }
    });
